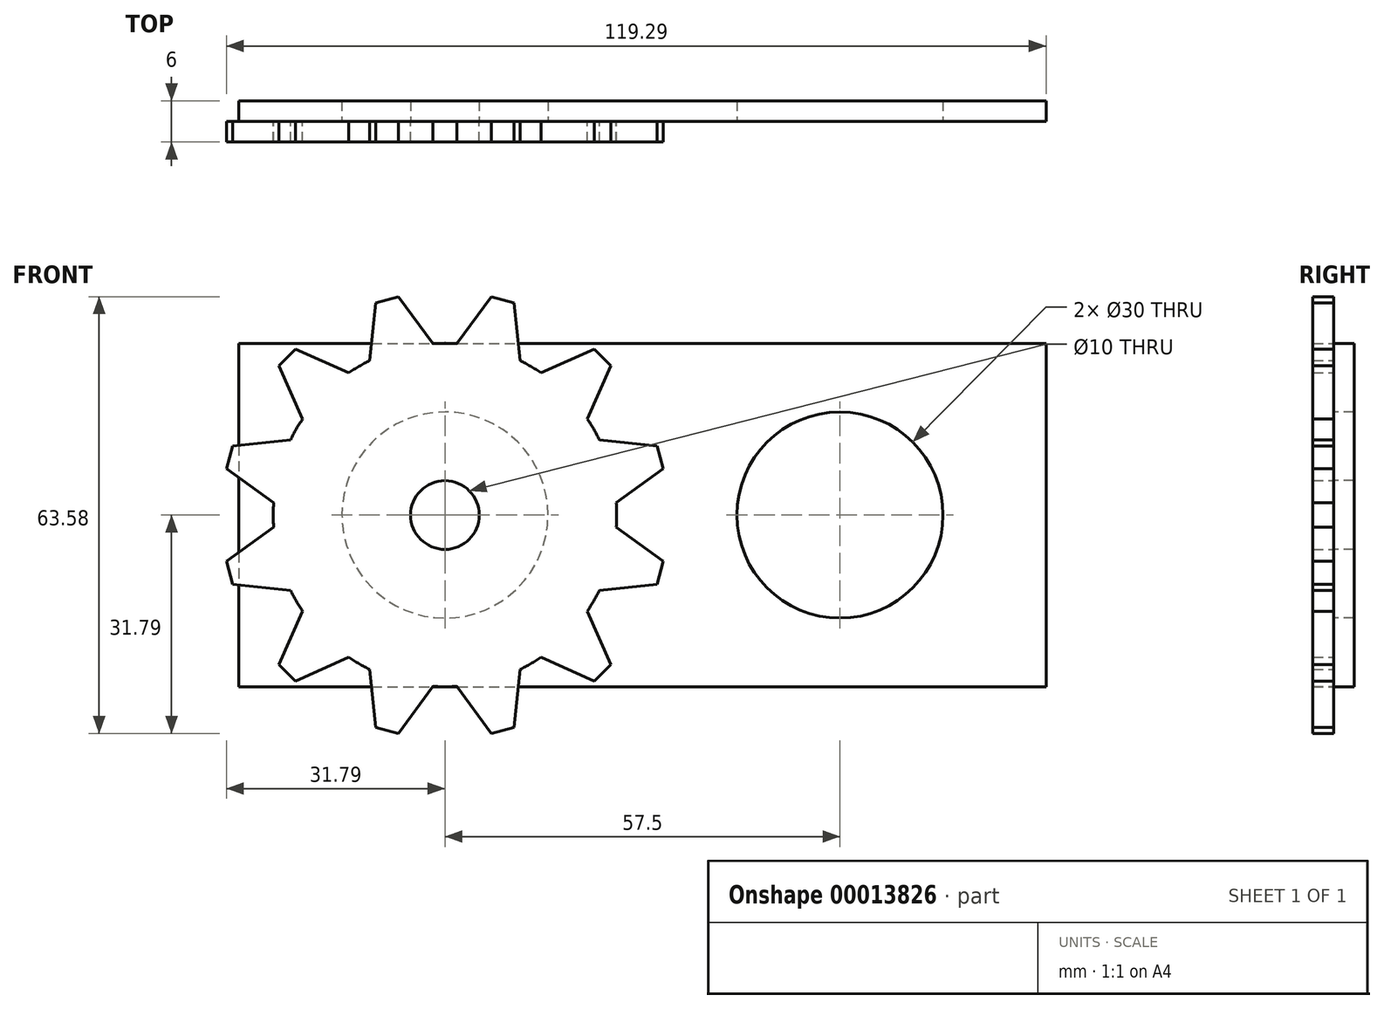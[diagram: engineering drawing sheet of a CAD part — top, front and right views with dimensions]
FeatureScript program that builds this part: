
annotation { "Feature Type Name" : "Feature", "Feature Type Description" : "" }
export const myFeature = defineFeature(function(context is Context, id is Id, definition is map)
    precondition{}
    {
        {
            var Q0;
            Q0=qCreatedBy(makeId("Front.planeOp"),FACE);
            var sketch = newSketch(context, id + "F7", { "sketchPlane" : qUnion([Q0])});
            skCircle(sketch, "E0", {"center": v(0, 0) * mm, "radius": 25 * mm, "construction": true});
            skLineSegment(sketch, "E1", {"start": v(0, 25) * mm, "end": v(12.5, 21.65) * mm, "construction": true});
            skLineSegment(sketch, "E2", {"start": v(6.25, 23.33) * mm, "end": v(8.83, 32.96) * mm, "construction": true});
            skLineSegment(sketch, "E3", {"start": v(0, 0) * mm, "end": v(0, 25) * mm, "construction": true});
            skLineSegment(sketch, "E4", {"start": v(0, 0) * mm, "end": v(12.5, 21.65) * mm, "construction": true});
            skCircle(sketch, "E5", {"center": v(0, 0) * mm, "radius": 32.5 * mm, "construction": true});
            skLineSegment(sketch, "E6", {"start": v(6.74, 31.8) * mm, "end": v(1.76, 24.94) * mm});
            skLineSegment(sketch, "E7.MirrorCS", {"start": v(10.06, 30.9) * mm, "end": v(10.94, 22.48) * mm});
            skLineSegment(sketch, "E8", {"start": v(6.74, 31.8) * mm, "end": v(10.06, 30.9) * mm});
            skLineSegment(sketch, "E9", {"start": v(1.76, 24.94) * mm, "end": v(10.94, 22.48) * mm});
            skSolve(sketch);
        }
        {
            var Q0;
            Q0 = qSketchRegion(id + "F7", true);
            extrude(context, id + "F0", {"entities" : qUnion([Q0]), "depth" : 3 * mm});
        }
        {
            var Q0;
            Q0=qCreatedBy(makeId("Top.planeOp"),FACE);
            var sketch = newSketch(context, id + "F8", { "sketchPlane" : qUnion([Q0])});
            skLineSegment(sketch, "E10", {"start": v(0, 0) * mm, "end": v(0, -32.55) * mm, "construction": true});
            skSolve(sketch);
        }
        {
            var Q0;
            Q0=qCreatedBy(makeId("Front.planeOp"),FACE);
            var sketch = newSketch(context, id + "F1", { "sketchPlane" : qUnion([Q0])});
            skCircle(sketch, "E11", {"center": v(0, 0) * mm, "radius": 25 * mm});
            skCircle(sketch, "E12", {"center": v(0, 0) * mm, "radius": 5 * mm});
            skSolve(sketch);
        }
        {
            var Q0;
            Q0 = qSketchRegion(id + "F1", true);
            extrude(context, id + "F2", {"entities" : qUnion([Q0]), "depth" : 3 * mm});
        }
        {
            var Q0;
            Q0=makeQuery(id+"F0.opExtrude","SWEPT_BODY",BODY,{"disambiguationData":[OSD([sQuery(id+"F7.wireOp",EDGE,"E6"),sQuery(id+"F7.wireOp",EDGE,"E7.MirrorCS"),sQuery(id+"F7.wireOp",EDGE,"E8"),sQuery(id+"F7.wireOp",EDGE,"E9")])]});
            var Q1;
            Q1=sQuery(id+"F8.wireOp",EDGE,"E10");
            circularPattern(context, id + "F9", {"operationType" : NewBodyOperationType.ADD, "entities" : qUnion([Q0]), "axis" : qUnion([Q1]), "angle" : 30 * degree, "instanceCount" : 12});
        }
        {
            var Q0;
            Q0=qCreatedBy(makeId("Front.planeOp"),FACE);
            var sketch = newSketch(context, id + "F3", { "sketchPlane" : qUnion([Q0])});
            skLineSegment(sketch, "E13.bottom", {"start": v(-30, 25) * mm, "end": v(87.5, 25) * mm});
            skLineSegment(sketch, "E13.top", {"start": v(-30, -25) * mm, "end": v(87.5, -25) * mm});
            skLineSegment(sketch, "E13.left", {"start": v(-30, 25) * mm, "end": v(-30, -25) * mm});
            skLineSegment(sketch, "E13.right", {"start": v(87.5, 25) * mm, "end": v(87.5, -25) * mm});
            skLineSegment(sketch, "E14", {"start": v(-30, 0) * mm, "end": v(87.5, 0) * mm, "construction": true});
            skCircle(sketch, "E15", {"center": v(0, 0) * mm, "radius": 15 * mm});
            skCircle(sketch, "E16", {"center": v(57.5, 0) * mm, "radius": 15 * mm});
            skLineSegment(sketch, "E17", {"start": v(0, 25) * mm, "end": v(0, 0) * mm, "construction": true});
            skSolve(sketch);
        }
        {
            var Q0;
            Q0 = qSketchRegion(id + "F3", true);
            extrude(context, id + "F4", {"entities" : qUnion([Q0]), "oppositeDirection" : true, "depth" : 3 * mm});
        }
        {
            var Q0;
            Q0=qCreatedBy(makeId("Front.planeOp"),FACE);
            var sketch = newSketch(context, id + "F5", { "sketchPlane" : qUnion([Q0])});
            skCircle(sketch, "E18", {"center": v(0, 0) * mm, "radius": 5 * mm});
            skSolve(sketch);
        }
        {
            var Q0;
            Q0 = qSketchRegion(id + "F5", true);
            extrude(context, id + "F6", {"entities" : qUnion([Q0]), "operationType" : NewBodyOperationType.ADD, "oppositeDirection" : true, "depth" : 3 * mm});
        }
    });
